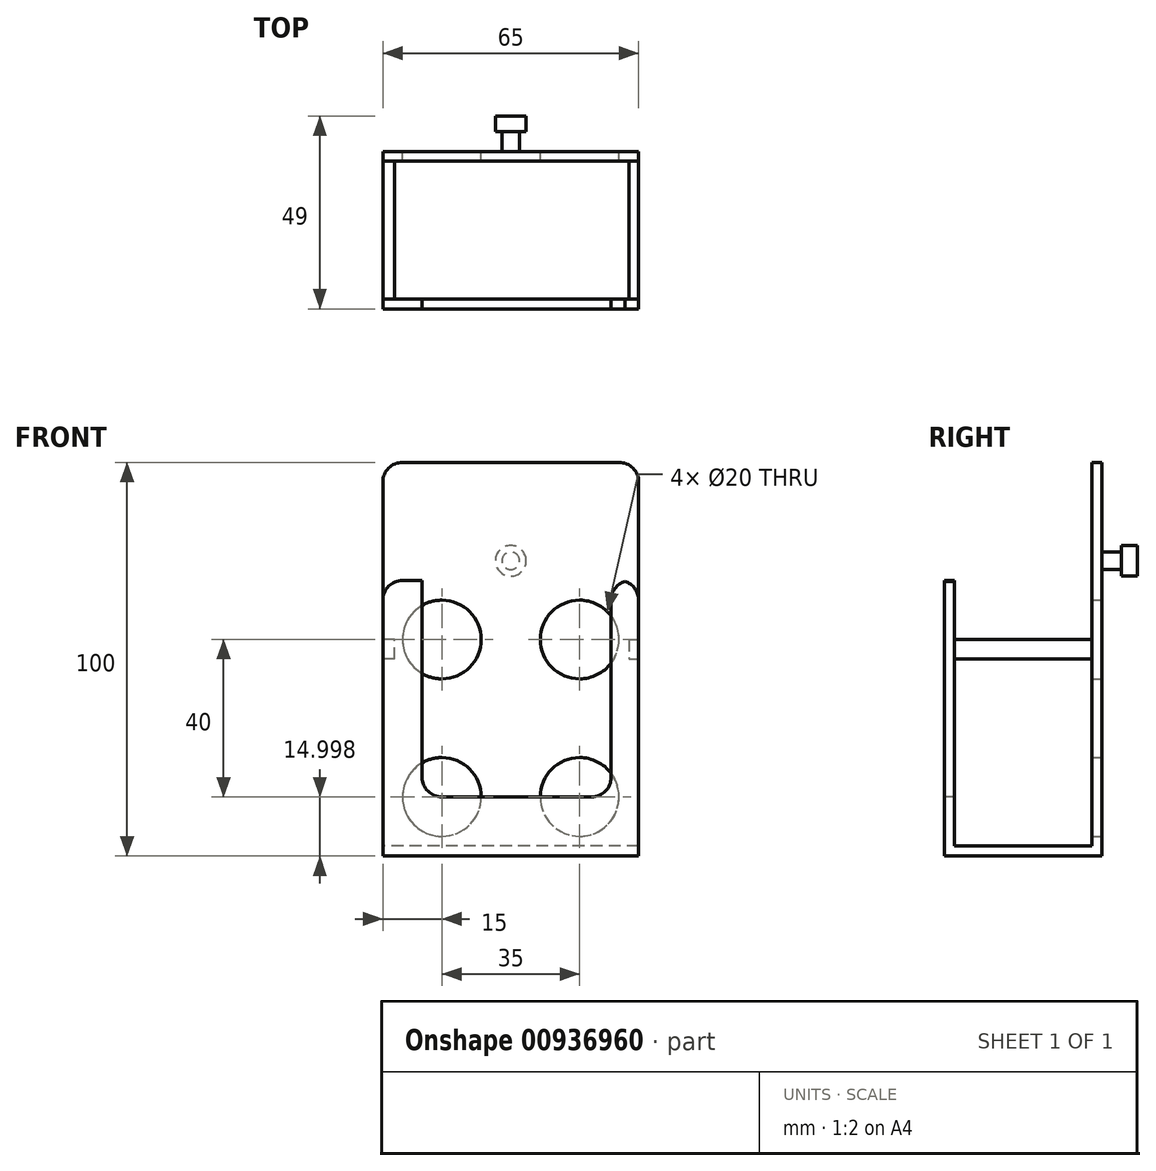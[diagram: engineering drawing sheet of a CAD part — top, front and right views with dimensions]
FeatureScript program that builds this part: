
annotation { "Feature Type Name" : "Feature", "Feature Type Description" : "" }
export const myFeature = defineFeature(function(context is Context, id is Id, definition is map)
    precondition{}
    {
        {
            var Q0;
            Q0=qCreatedBy(makeId("Right.planeOp"),FACE);
            var sketch = newSketch(context, id + "F0", { "sketchPlane" : qUnion([Q0])});
            skLineSegment(sketch, "E0", {"start": v(0, 65.07) * mm, "end": v(0, -34.93) * mm});
            skLineSegment(sketch, "E1", {"start": v(0, -34.93) * mm, "end": v(-40, -34.93) * mm});
            skLineSegment(sketch, "E2", {"start": v(-40, -34.93) * mm, "end": v(-40, 35.07) * mm});
            skLineSegment(sketch, "E3", {"start": v(-40, 35.07) * mm, "end": v(-37.5, 35.07) * mm});
            skLineSegment(sketch, "E4", {"start": v(-37.5, 35.07) * mm, "end": v(-37.5, -32.43) * mm});
            skLineSegment(sketch, "E5", {"start": v(-37.5, -32.43) * mm, "end": v(-2.5, -32.43) * mm});
            skLineSegment(sketch, "E6", {"start": v(-2.5, -32.43) * mm, "end": v(-2.5, 65.07) * mm});
            skLineSegment(sketch, "E7", {"start": v(-2.5, 65.07) * mm, "end": v(0, 65.07) * mm});
            skSolve(sketch);
        }
        {
            var Q0;
            Q0=makeQuery(id+"F0.imprint","IMPRINT",FACE,{"disambiguationData":[TD([[makeQuery(id+"F0.imprint","IMPRINT",EDGE,{"derivedFrom":sQuery(id+"F0.wireOp",EDGE,"E0")}),-1.0]])]});
            extrude(context, id + "F1", {"entities" : qUnion([Q0]), "depth" : 65 * mm, "offsetDistance" : 25 * mm});
        }
        {
            var Q0;
            Q0=makeQuery(id+"F1.opExtrude","SWEPT_FACE",FACE,{"disambiguationData":[OSD([sQuery(id+"F0.wireOp",EDGE,"E2")])]});
            var sketch = newSketch(context, id + "F2", { "sketchPlane" : qUnion([Q0])});
            skLineSegment(sketch, "E8", {"start": v(10, 108.09) * mm, "end": v(10, -72.04) * mm, "construction": true});
            skLineSegment(sketch, "E9", {"start": v(58, 106.4) * mm, "end": v(58, -94.08) * mm, "construction": true});
            skLineSegment(sketch, "E10", {"start": v(-56, -19.93) * mm, "end": v(151.26, -19.93) * mm, "construction": true});
            skLineSegment(sketch, "E11", {"start": v(10, 35.07) * mm, "end": v(10, -19.93) * mm});
            skLineSegment(sketch, "E12", {"start": v(10, -19.93) * mm, "end": v(58, -19.93) * mm});
            skLineSegment(sketch, "E13", {"start": v(58, -19.93) * mm, "end": v(58, 35.07) * mm});
            skLineSegment(sketch, "E14", {"start": v(58, 35.07) * mm, "end": v(10, 35.07) * mm});
            skSolve(sketch);
        }
        {
            var Q0;
            Q0=makeQuery(id+"F2.imprint","IMPRINT",FACE,{"disambiguationData":[TD([[makeQuery(id+"F2.imprint","IMPRINT",EDGE,{"derivedFrom":sQuery(id+"F2.wireOp",EDGE,"E11")}),1.0]])]});
            extrude(context, id + "F3", {"entities" : qUnion([Q0]), "operationType" : NewBodyOperationType.REMOVE, "oppositeDirection" : true, "depth" : 10 * mm, "offsetDistance" : 25 * mm});
        }
        {
            var Q0;
            Q0=makeQuery(id+"F1.opExtrude","SWEPT_FACE",FACE,{"disambiguationData":[OSD([sQuery(id+"F0.wireOp",EDGE,"E0")])]});
            var sketch = newSketch(context, id + "F4", { "sketchPlane" : qUnion([Q0])});
            skLineSegment(sketch, "E15", {"start": v(-32.5, 65.07) * mm, "end": v(-32.5, -75.25) * mm, "construction": true});
            skLineSegment(sketch, "E16", {"start": v(32.91, 40.07) * mm, "end": v(-91.6, 40.07) * mm, "construction": true});
            skCircle(sketch, "E17", {"center": v(-32.5, 40.07) * mm, "radius": 2.25 * mm});
            skSolve(sketch);
        }
        {
            var Q0;
            Q0=makeQuery(id+"F4.imprint","IMPRINT",FACE,{"disambiguationData":[TD([[makeQuery(id+"F4.imprint","IMPRINT",EDGE,{"derivedFrom":sQuery(id+"F4.wireOp",EDGE,"E17")}),1.0]])]});
            extrude(context, id + "F5", {"entities" : qUnion([Q0]), "operationType" : NewBodyOperationType.ADD, "depth" : 5 * mm, "offsetDistance" : 25 * mm});
        }
        {
            var Q0;
            Q0=makeQuery(id+"F5.opExtrude","CAP_FACE",FACE,{"disambiguationData":[OSD([sQuery(id+"F4.wireOp",EDGE,"E17")])],"isStart":false});
            var sketch = newSketch(context, id + "F6", { "sketchPlane" : qUnion([Q0])});
            skCircle(sketch, "E18", {"center": v(-32.5, 40.07) * mm, "radius": 3.9 * mm});
            skSolve(sketch);
        }
        {
            var Q0;
            Q0=makeQuery(id+"F6.imprint","IMPRINT",FACE,{"disambiguationData":[TD([[makeQuery(id+"F6.imprint","IMPRINT",EDGE,{"derivedFrom":makeQuery(id+"F5.opExtrude","CAP_EDGE",EDGE,{"disambiguationData":[OSD([sQuery(id+"F4.wireOp",EDGE,"E17")])],"isStart":false})}),1.0]])]});
            var Q1;
            Q1=makeQuery(id+"F6.imprint","IMPRINT",FACE,{"disambiguationData":[TD([[makeQuery(id+"F6.imprint","IMPRINT",EDGE,{"derivedFrom":sQuery(id+"F6.wireOp",EDGE,"E18")}),1.0]])]});
            extrude(context, id + "F7", {"entities" : qUnion([Q0, Q1]), "operationType" : NewBodyOperationType.ADD, "depth" : 4 * mm, "offsetDistance" : 25 * mm});
        }
        {
            var Q0;
            Q0=makeQuery(id+"F1.opExtrude","SWEPT_FACE",FACE,{"disambiguationData":[OSD([sQuery(id+"F0.wireOp",EDGE,"E0")])]});
            var sketch = newSketch(context, id + "F8", { "sketchPlane" : qUnion([Q0])});
            skLineSegment(sketch, "E19", {"start": v(-76.89, 20.07) * mm, "end": v(46.89, 20.07) * mm, "construction": true});
            skLineSegment(sketch, "E20", {"start": v(-78.71, -19.93) * mm, "end": v(48.71, -19.93) * mm, "construction": true});
            skLineSegment(sketch, "E21", {"start": v(-50, 35.05) * mm, "end": v(-50, -46.5) * mm, "construction": true});
            skLineSegment(sketch, "E22", {"start": v(-15, 35.65) * mm, "end": v(-15, -45.58) * mm, "construction": true});
            skCircle(sketch, "E23", {"center": v(-50, 20.07) * mm, "radius": 10 * mm});
            skCircle(sketch, "E24", {"center": v(-15, 20.07) * mm, "radius": 10 * mm});
            skCircle(sketch, "E25", {"center": v(-15, -19.93) * mm, "radius": 10 * mm});
            skCircle(sketch, "E26", {"center": v(-50, -19.93) * mm, "radius": 10 * mm});
            skSolve(sketch);
        }
        {
            var Q0;
            Q0=makeQuery(id+"F8.imprint","IMPRINT",FACE,{"disambiguationData":[TD([[makeQuery(id+"F8.imprint","IMPRINT",EDGE,{"derivedFrom":sQuery(id+"F8.wireOp",EDGE,"E23")}),1.0]])]});
            var Q1;
            Q1=makeQuery(id+"F8.imprint","IMPRINT",FACE,{"disambiguationData":[TD([[makeQuery(id+"F8.imprint","IMPRINT",EDGE,{"derivedFrom":sQuery(id+"F8.wireOp",EDGE,"E24")}),1.0]])]});
            var Q2;
            Q2=makeQuery(id+"F8.imprint","IMPRINT",FACE,{"disambiguationData":[TD([[makeQuery(id+"F8.imprint","IMPRINT",EDGE,{"derivedFrom":sQuery(id+"F8.wireOp",EDGE,"E25")}),1.0]])]});
            var Q3;
            Q3=makeQuery(id+"F8.imprint","IMPRINT",FACE,{"disambiguationData":[TD([[makeQuery(id+"F8.imprint","IMPRINT",EDGE,{"derivedFrom":sQuery(id+"F8.wireOp",EDGE,"E26")}),1.0]])]});
            extrude(context, id + "F9", {"entities" : qUnion([Q0, Q1, Q2, Q3]), "operationType" : NewBodyOperationType.REMOVE, "oppositeDirection" : true, "depth" : 4 * mm, "offsetDistance" : 25 * mm});
        }
        {
            var Q0;
            Q0=makeQuery(id+"F1.opExtrude","CAP_FACE",FACE,{"disambiguationData":[OSD([sQuery(id+"F0.wireOp",EDGE,"E0"),sQuery(id+"F0.wireOp",EDGE,"E1"),sQuery(id+"F0.wireOp",EDGE,"E2"),sQuery(id+"F0.wireOp",EDGE,"E3"),sQuery(id+"F0.wireOp",EDGE,"E4"),sQuery(id+"F0.wireOp",EDGE,"E5"),sQuery(id+"F0.wireOp",EDGE,"E6"),sQuery(id+"F0.wireOp",EDGE,"E7")])],"isStart":false});
            var sketch = newSketch(context, id + "F10", { "sketchPlane" : qUnion([Q0])});
            skLineSegment(sketch, "E27", {"start": v(-40, 20.07) * mm, "end": v(0, 20.07) * mm});
            skLineSegment(sketch, "E28", {"start": v(-40, 15.07) * mm, "end": v(0, 15.07) * mm});
            skSolve(sketch);
        }
        {
            var Q0;
            {var subQ0=sQuery(id+"F10.wireOp",EDGE,"E27");var subQ1=makeQuery(id+"F1.opExtrude","CAP_EDGE",EDGE,{"disambiguationData":[OSD([sQuery(id+"F0.wireOp",EDGE,"E4")])],"isStart":false});var subQ2=makeQuery(id+"F10.imprint","INTERSECT",VERTEX,{"derivedFrom":[subQ1,subQ0]});Q0=makeQuery(id+"F10.imprint","IMPRINT",FACE,{"disambiguationData":[TD([[makeQuery(id+"F10.imprint","IMPRINT",EDGE,{"disambiguationData":[TD([[subQ2,-1.0]])],"derivedFrom":subQ0}),-1.0]])]});}
            extrude(context, id + "F11", {"entities" : qUnion([Q0]), "oppositeDirection" : true, "depth" : 2.5 * mm, "offsetDistance" : 25 * mm});
        }
        {
            var Q0;
            Q0=makeQuery(id+"F1.opExtrude","CAP_FACE",FACE,{"disambiguationData":[OSD([sQuery(id+"F0.wireOp",EDGE,"E0"),sQuery(id+"F0.wireOp",EDGE,"E1"),sQuery(id+"F0.wireOp",EDGE,"E2"),sQuery(id+"F0.wireOp",EDGE,"E3"),sQuery(id+"F0.wireOp",EDGE,"E4"),sQuery(id+"F0.wireOp",EDGE,"E5"),sQuery(id+"F0.wireOp",EDGE,"E6"),sQuery(id+"F0.wireOp",EDGE,"E7")])],"isStart":true});
            var sketch = newSketch(context, id + "F12", { "sketchPlane" : qUnion([Q0])});
            skLineSegment(sketch, "E29", {"start": v(0, 20.07) * mm, "end": v(40, 20.07) * mm});
            skLineSegment(sketch, "E30", {"start": v(0, 15.07) * mm, "end": v(40, 15.07) * mm});
            skSolve(sketch);
        }
        {
            var Q0;
            {var subQ0=sQuery(id+"F12.wireOp",EDGE,"E29");var subQ1=makeQuery(id+"F1.opExtrude","CAP_EDGE",EDGE,{"disambiguationData":[OSD([sQuery(id+"F0.wireOp",EDGE,"E6")])],"isStart":true});var subQ2=makeQuery(id+"F12.imprint","INTERSECT",VERTEX,{"derivedFrom":[subQ1,subQ0]});Q0=makeQuery(id+"F12.imprint","IMPRINT",FACE,{"disambiguationData":[TD([[makeQuery(id+"F12.imprint","IMPRINT",EDGE,{"disambiguationData":[TD([[subQ2,-1.0]])],"derivedFrom":subQ0}),-1.0]])]});}
            extrude(context, id + "F13", {"entities" : qUnion([Q0]), "oppositeDirection" : true, "depth" : 3 * mm, "offsetDistance" : 25 * mm});
        }
        {
            var Q0;
            Q0=makeQuery(id+"F1.opExtrude","CAP_EDGE",EDGE,{"disambiguationData":[OSD([sQuery(id+"F0.wireOp",EDGE,"E3")])],"isStart":true});
            var Q1;
            Q1=makeQuery(id+"F3.boolean.opBoolean","COPY",EDGE,{"derivedFrom":makeQuery(id+"F3.opExtrude","SWEPT_EDGE",EDGE,{"disambiguationData":[OSD([sQuery(id+"F0.wireOp",EDGE,"E2"),sQuery(id+"F0.wireOp",EDGE,"E3"),sQuery(id+"F2.wireOp",EDGE,"E11"),sQuery(id+"F2.wireOp",EDGE,"E14")])]})});
            var Q2;
            Q2=makeQuery(id+"F3.boolean.opBoolean","COPY",EDGE,{"derivedFrom":makeQuery(id+"F3.opExtrude","SWEPT_EDGE",EDGE,{"disambiguationData":[OSD([sQuery(id+"F0.wireOp",EDGE,"E2"),sQuery(id+"F0.wireOp",EDGE,"E3"),sQuery(id+"F2.wireOp",EDGE,"E13"),sQuery(id+"F2.wireOp",EDGE,"E14")])]})});
            var Q3;
            Q3=makeQuery(id+"F1.opExtrude","CAP_EDGE",EDGE,{"disambiguationData":[OSD([sQuery(id+"F0.wireOp",EDGE,"E3")])],"isStart":false});
            var Q4;
            Q4=makeQuery(id+"F1.opExtrude","CAP_EDGE",EDGE,{"disambiguationData":[OSD([sQuery(id+"F0.wireOp",EDGE,"E7")])],"isStart":false});
            var Q5;
            Q5=makeQuery(id+"F1.opExtrude","CAP_EDGE",EDGE,{"disambiguationData":[OSD([sQuery(id+"F0.wireOp",EDGE,"E7")])],"isStart":true});
            var Q6;
            Q6=makeQuery(id+"F3.boolean.opBoolean","COPY",EDGE,{"derivedFrom":makeQuery(id+"F3.opExtrude","SWEPT_EDGE",EDGE,{"disambiguationData":[OSD([sQuery(id+"F2.wireOp",EDGE,"E11"),sQuery(id+"F2.wireOp",EDGE,"E12")])]})});
            var Q7;
            Q7=makeQuery(id+"F3.boolean.opBoolean","COPY",EDGE,{"derivedFrom":makeQuery(id+"F3.opExtrude","SWEPT_EDGE",EDGE,{"disambiguationData":[OSD([sQuery(id+"F2.wireOp",EDGE,"E12"),sQuery(id+"F2.wireOp",EDGE,"E13")])]})});
            fillet(context, id + "F14", {"entities" : qUnion([Q0, Q1, Q2, Q3, Q4, Q5, Q6, Q7]), "radius" : 5 * mm, "tangentPropagation" : true, "allowEdgeOverflow" : false});
        }
    });
